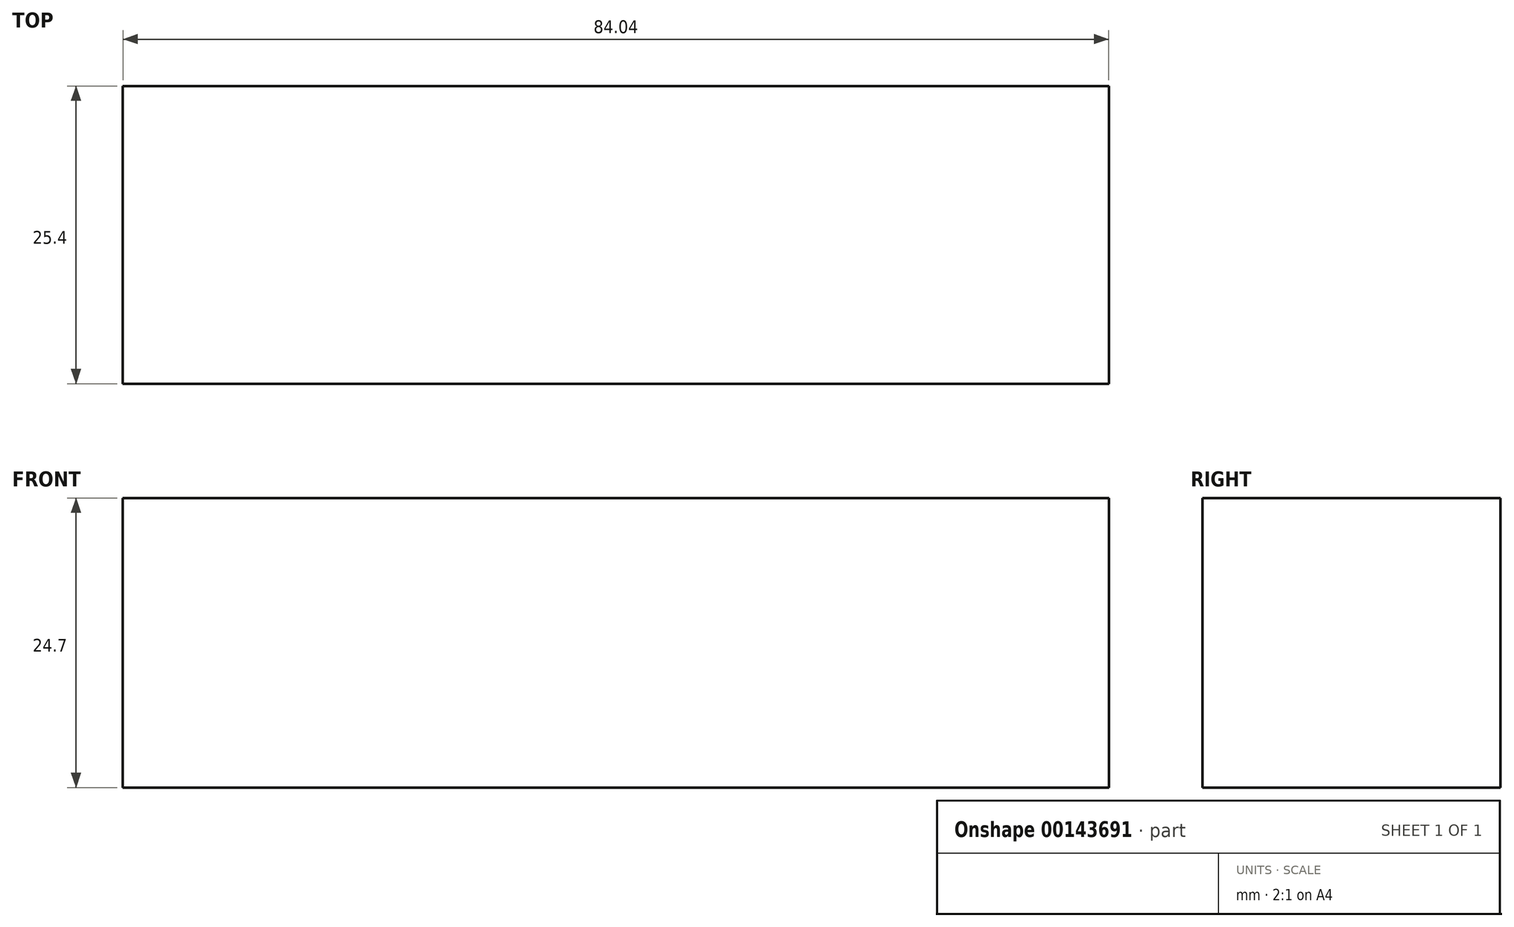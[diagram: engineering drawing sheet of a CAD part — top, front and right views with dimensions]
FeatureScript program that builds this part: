
annotation { "Feature Type Name" : "Feature", "Feature Type Description" : "" }
export const myFeature = defineFeature(function(context is Context, id is Id, definition is map)
    precondition{}
    {
        {
            var Q0;
            Q0=qCreatedBy(makeId("Front.planeOp"),FACE);
            var sketch = newSketch(context, id + "F0", { "sketchPlane" : qUnion([Q0])});
            skLineSegment(sketch, "E0.bottom", {"start": v(-42.02, 12.35) * mm, "end": v(42.02, 12.35) * mm});
            skLineSegment(sketch, "E0.top", {"start": v(-42.02, -12.35) * mm, "end": v(42.02, -12.35) * mm});
            skLineSegment(sketch, "E0.left", {"start": v(-42.02, 12.35) * mm, "end": v(-42.02, -12.35) * mm});
            skLineSegment(sketch, "E0.right", {"start": v(42.02, 12.35) * mm, "end": v(42.02, -12.35) * mm});
            skPoint(sketch, "E0.middle", {"position": v(0, 0) * mm});
            skSolve(sketch);
        }
        {
            var Q0;
            Q0 = qSketchRegion(id + "F0", true);
            extrude(context, id + "F1", {"entities" : qUnion([Q0]), "endBound" : BoundingType.SYMMETRIC, "depth" : 25.4 * mm});
        }
    });
